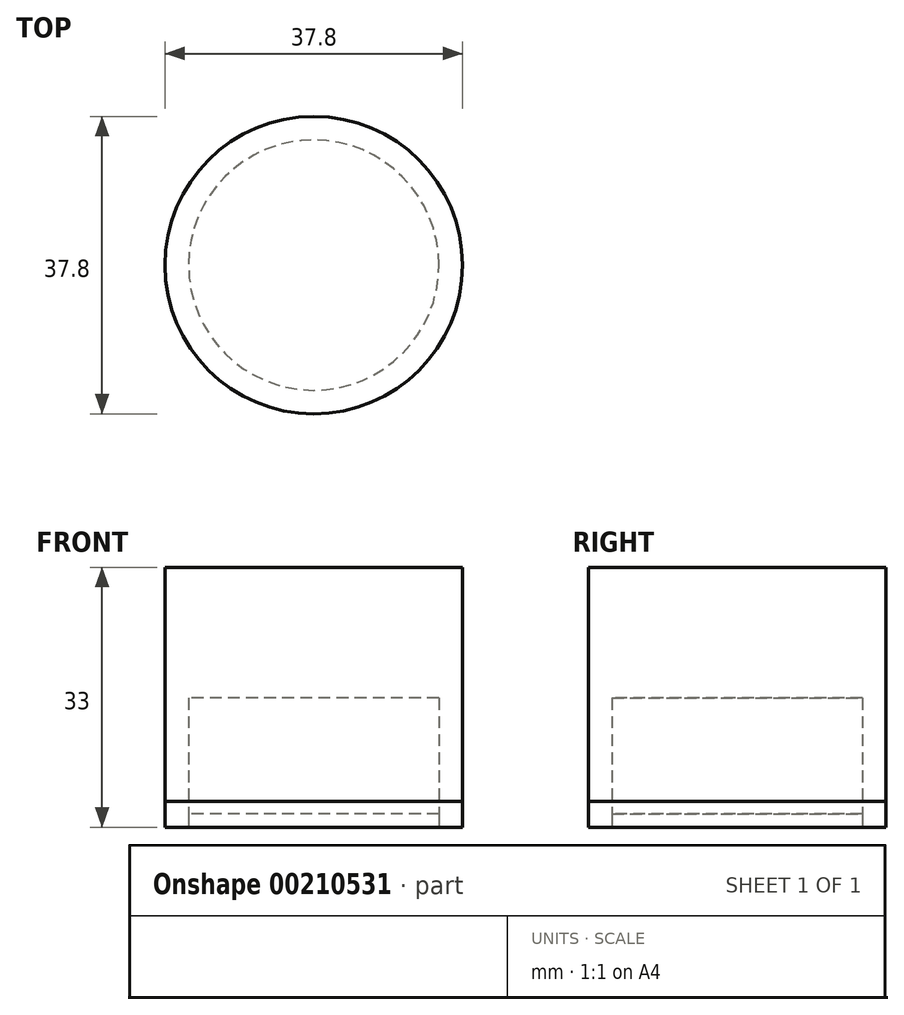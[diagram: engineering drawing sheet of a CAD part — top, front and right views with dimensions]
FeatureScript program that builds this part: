
annotation { "Feature Type Name" : "Feature", "Feature Type Description" : "" }
export const myFeature = defineFeature(function(context is Context, id is Id, definition is map)
    precondition{}
    {
        {
            var Q0;
            Q0=qCreatedBy(makeId("Top.planeOp"),FACE);
            var sketch = newSketch(context, id + "F0", { "sketchPlane" : qUnion([Q0])});
            skCircle(sketch, "E0", {"center": v(0, 0) * mm, "radius": 18.9 * mm});
            skSolve(sketch);
        }
        {
            var Q0;
            Q0=qSketchRegion(id+"F0",true);
            extrude(context, id + "F1", {"entities" : qUnion([Q0]), "depth" : 3.3 * mm});
        }
        {
            var Q0;
            Q0=qCreatedBy(makeId("Top.planeOp"),FACE);
            var sketch = newSketch(context, id + "F2", { "sketchPlane" : qUnion([Q0])});
            skCircle(sketch, "E1", {"center": v(0, 0) * mm, "radius": 15.9 * mm});
            skSolve(sketch);
        }
        {
            var Q0;
            Q0=qSketchRegion(id+"F2",true);
            extrude(context, id + "F3", {"entities" : qUnion([Q0]), "depth" : 1.7 * mm});
        }
        {
            var Q0;
            Q0=makeQuery(id+"F2.imprint","IMPRINT",FACE,{"disambiguationData":[TD([[makeQuery(id+"F2.imprint","IMPRINT",EDGE,{"derivedFrom":sQuery(id+"F2.wireOp",EDGE,"E1")}),1.0]])]});
            var Q1;
            Q1=sQuery(id+"F2.wireOp",EDGE,"E1");
            extrude(context, id + "F4", {"entities" : qUnion([Q0]), "surfaceEntities" : qUnion([Q1]), "depth" : 16.4 * mm});
        }
        {
            var Q0;
            Q0=makeQuery(id+"F0.imprint","IMPRINT",FACE,{"disambiguationData":[TD([[makeQuery(id+"F0.imprint","IMPRINT",EDGE,{"derivedFrom":sQuery(id+"F0.wireOp",EDGE,"E0")}),1.0]])]});
            extrude(context, id + "F5", {"entities" : qUnion([Q0]), "depth" : 33 * mm});
        }
    });
